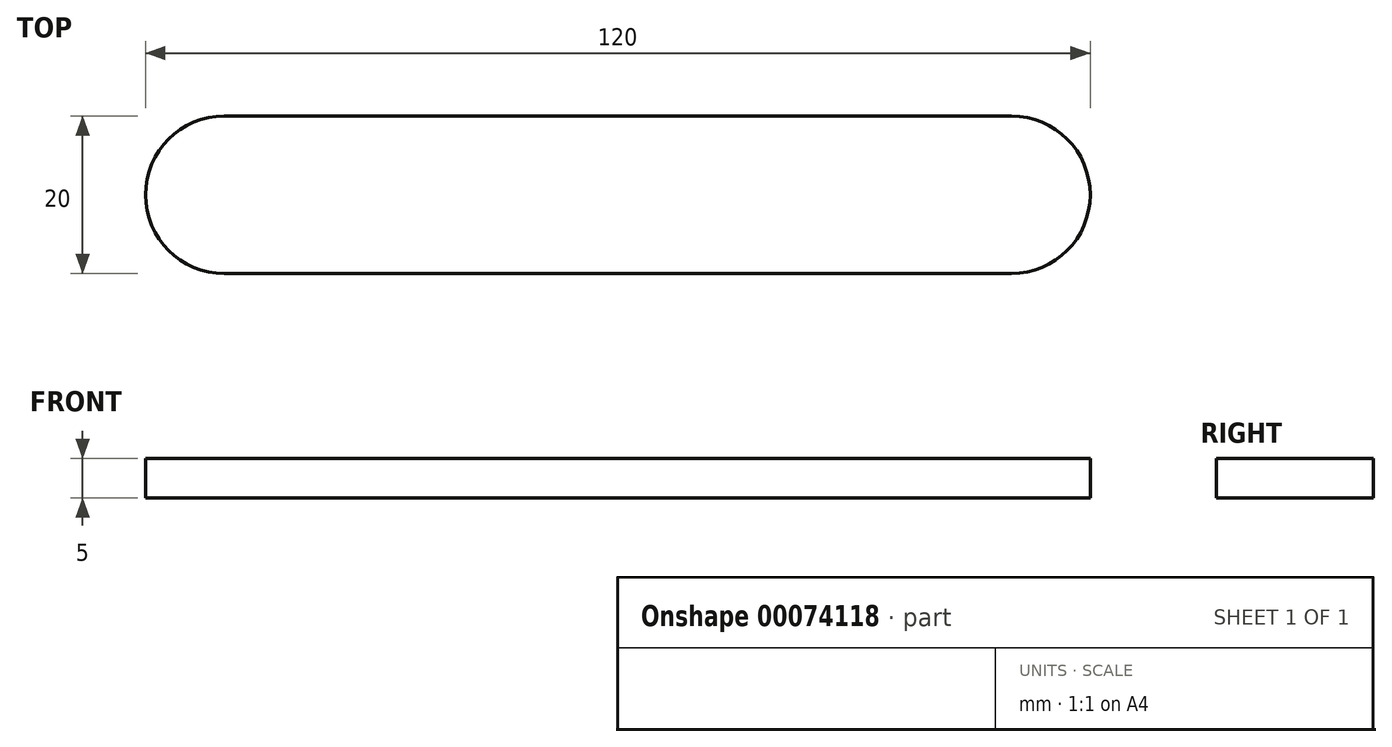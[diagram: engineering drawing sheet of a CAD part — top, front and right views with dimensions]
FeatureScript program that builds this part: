
annotation { "Feature Type Name" : "Feature", "Feature Type Description" : "" }
export const myFeature = defineFeature(function(context is Context, id is Id, definition is map)
    precondition{}
    {
        {
            var Q0;
            Q0=qCreatedBy(makeId("Top.planeOp"),FACE);
            var sketch = newSketch(context, id + "F0", { "sketchPlane" : qUnion([Q0])});
            skLineSegment(sketch, "E0.rect.bottom", {"start": v(50, 10) * mm, "end": v(-50, 10) * mm});
            skLineSegment(sketch, "E0.rect.top", {"start": v(50, -10) * mm, "end": v(-50, -10) * mm});
            skLineSegment(sketch, "E0.rect.left", {"start": v(50, 10) * mm, "end": v(50, -10) * mm});
            skLineSegment(sketch, "E0.rect.right", {"start": v(-50, 10) * mm, "end": v(-50, -10) * mm});
            skPoint(sketch, "E0.rect.middle", {"position": v(0, 0) * mm});
            skCircle(sketch, "E1", {"center": v(50, 0) * mm, "radius": 10 * mm});
            skCircle(sketch, "E2", {"center": v(-50, 0) * mm, "radius": 10 * mm});
            skSolve(sketch);
        }
        {
            var Q0;
            Q0 = qSketchRegion(id + "F0", true);
            extrude(context, id + "F1", {"entities" : qUnion([Q0]), "depth" : 5 * mm});
        }
    });
